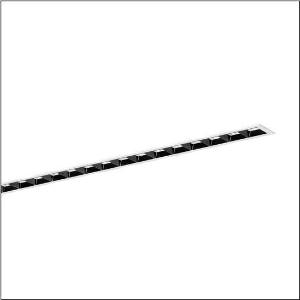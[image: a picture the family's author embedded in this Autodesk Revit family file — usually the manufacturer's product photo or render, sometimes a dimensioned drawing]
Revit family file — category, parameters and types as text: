
# Revit family: silica_21_51mx14dc3awb
name_source: partatom
category: Lighting Fixtures
units: mm (PartAtom-declared; Revit-internal decimal feet)

## family parameters
Cut with Voids When Loaded = No
Host = Face
Light Source = No
Part Type = Normal
Room Calculation Point = No
Round Connector Dimension = Use Diameter
Shared = No

## types (1)
- --- (1 x LED, 10800 lm, 79 W, 3000K)
    Apparent Load = 79 VA
    CIE Flux Codes = 74 94 99 100 100
    Color Rendering = 80
    Color Temperature = 3000K
    Default Elevation = 1800 mm
    Description = Silica 21, office luminaire, primary light control with darklight reflector, of PMMA, black, light emission: direct distribution, primary light characteristic: asymmetric, installation type: recessed, LED, rated luminous flux: 10.800lm, luminous efficacy: 137lm/W, light colour: 830, colour temperature: 3000K, control gear: DALI 2, with terminal, 3+2-pole, max. 2.5mm², mains connection: 220..240V, AC, 50/60Hz, rated input power: 79W, luminaire housing, of aluminium, traffic white (RAL 9016), length: 3.028mm, width: 79mm, height: 53mm, protection rating (complete): IP20, insulation class (complete): insulation class I (protective earthing), certification: CE, ENEC, VDE, permissible operating ambient temperature: 0..+35°C, standard: EN 50419, packaging unit: 1 piece
    Height = 0 mm  [stored 0 ft]
    Lamp = 1 x LED
    Lamp Light Flux = 10800 lm
    Lamp Power = 79 W
    Lamp count = 1
    Length = 3027 mm
    Luminous efficacy = 137 lm/W
    Manufacturer = Siteco
    ModVariant = No
    Model = 51MX14DC3AWB
    Mounting Place = Ceiling
    Mounting Type = Recessed
    Number of Poles = 1
    OnlyDefault = Yes
    Power Factor = 1
    Product Name = Silica 21
    Product group = office luminaire | ceiling recessed
    ProductGroupID = 400
    Protection Class = Protection class I
    Protection Degree = IP 20
    RLX_Detail_Level = 1
    RLX_Emergency_Light_Flux = 0 lm
    RLX_Emergency_Type = 0
    RLX_Emergency_Type_DB = No
    RlxData = <blob elided: 63337 chars, md5=5b4c398b>
    Socket = socket
    Standby Power = 0 W
    System Light Flux = 10800 lm
    System Power = 79 W
    Type Comments = factory setting: luminous flux: 100 % | dim-lin: 254 | 448 mA
    Type Image = l_1335880.jpg
    URL = http://relux.com
    VarID = @adj_124043
    Voltage = 0 V
    Weight = 0.00 kg
    Width = 79 mm

note: [stored X ft] marks values corroborated as IEEE doubles in the binary element streams (Revit-internal decimal feet)

## geometry (parser evidence)
native form markers: Blend x4, Sweep x10
no freeform markers — native parametric forms only
